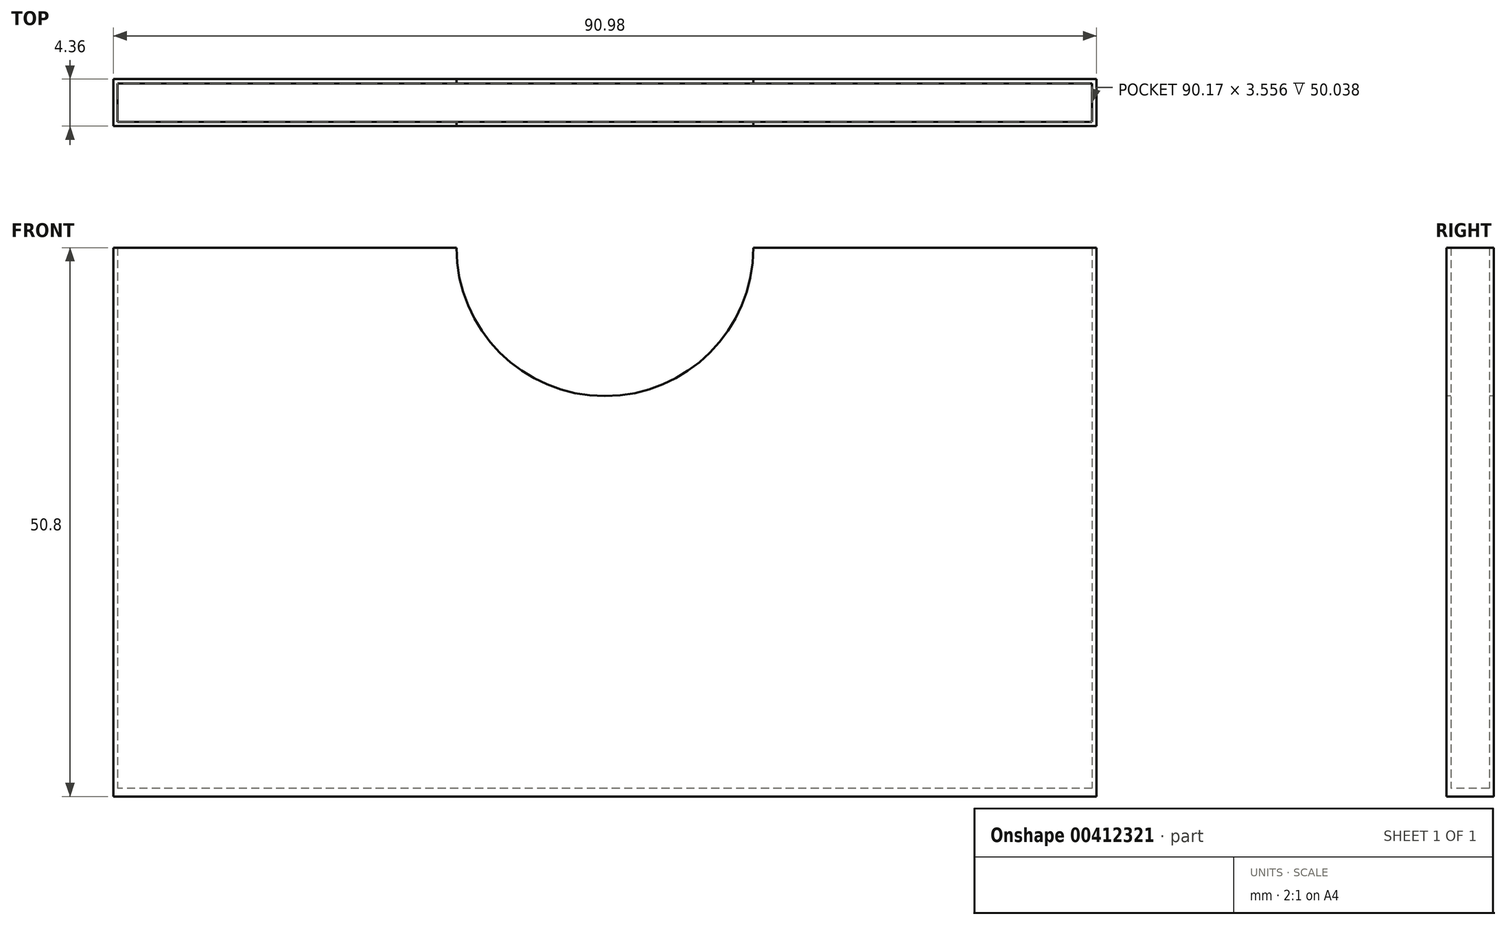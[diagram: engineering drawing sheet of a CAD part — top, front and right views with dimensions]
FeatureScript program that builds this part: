
annotation { "Feature Type Name" : "Feature", "Feature Type Description" : "" }
export const myFeature = defineFeature(function(context is Context, id is Id, definition is map)
    precondition{}
    {
        {
            var Q0;
            Q0=qCreatedBy(makeId("Top.planeOp"),FACE);
            var sketch = newSketch(context, id + "F0", { "sketchPlane" : qUnion([Q0])});
            skLineSegment(sketch, "E0.bottom", {"start": v(45.09, 1.78) * mm, "end": v(-45.09, 1.78) * mm});
            skLineSegment(sketch, "E0.top", {"start": v(45.09, -1.78) * mm, "end": v(-45.09, -1.78) * mm});
            skLineSegment(sketch, "E0.left", {"start": v(45.09, 1.78) * mm, "end": v(45.09, -1.78) * mm});
            skLineSegment(sketch, "E0.right", {"start": v(-45.09, 1.78) * mm, "end": v(-45.09, -1.78) * mm});
            skPoint(sketch, "E0.middle", {"position": v(0, 0) * mm});
            skLineSegment(sketch, "E1.bottom", {"start": v(-45.5, 2.18) * mm, "end": v(45.5, 2.18) * mm});
            skLineSegment(sketch, "E1.top", {"start": v(-45.5, -2.18) * mm, "end": v(45.5, -2.18) * mm});
            skLineSegment(sketch, "E1.left", {"start": v(-45.5, 2.18) * mm, "end": v(-45.5, -2.18) * mm});
            skLineSegment(sketch, "E1.right", {"start": v(45.5, 2.18) * mm, "end": v(45.5, -2.18) * mm});
            skSolve(sketch);
        }
        {
            var Q0;
            Q0=qSketchRegion(id+"F0",true);
            extrude(context, id + "F1", {"entities" : qUnion([Q0]), "depth" : 50.8 * mm});
        }
        {
            var Q0;
            Q0=qSketchRegion(id+"F0",true);
            var Q1;
            Q1=makeQuery(id+"F0.imprint","IMPRINT",FACE,{"disambiguationData":[TD([[makeQuery(id+"F0.imprint","IMPRINT",EDGE,{"derivedFrom":sQuery(id+"F0.wireOp",EDGE,"E0.bottom")}),1.0]])]});
            extrude(context, id + "F2", {"entities" : qUnion([Q0, Q1]), "operationType" : NewBodyOperationType.ADD, "depth" : 0.76 * mm});
        }
        {
            var Q0;
            Q0=makeQuery(id+"F1.opExtrude","SWEPT_FACE",FACE,{"disambiguationData":[OSD([sQuery(id+"F0.wireOp",EDGE,"E1.top")])]});
            var sketch = newSketch(context, id + "F3", { "sketchPlane" : qUnion([Q0])});
            skArc(sketch, "E2", {"start": v(-13.74, 50.8) * mm, "mid": v(0, 37.06) * mm, "end": v(13.74, 50.8) * mm});
            skSolve(sketch);
        }
        {
            var Q0;
            {var subQ0=sQuery(id+"F3.wireOp",EDGE,"E2");Q0=makeQuery(id+"F3.imprint","IMPRINT",FACE,{"disambiguationData":[TD([[makeQuery(id+"F3.imprint","IMPRINT",EDGE,{"derivedFrom":subQ0}),1.0]])]});}
            extrude(context, id + "F4", {"entities" : qUnion([Q0]), "operationType" : NewBodyOperationType.REMOVE, "endBound" : BoundingType.THROUGH_ALL, "oppositeDirection" : true, "depth" : 25.4 * mm});
        }
    });
